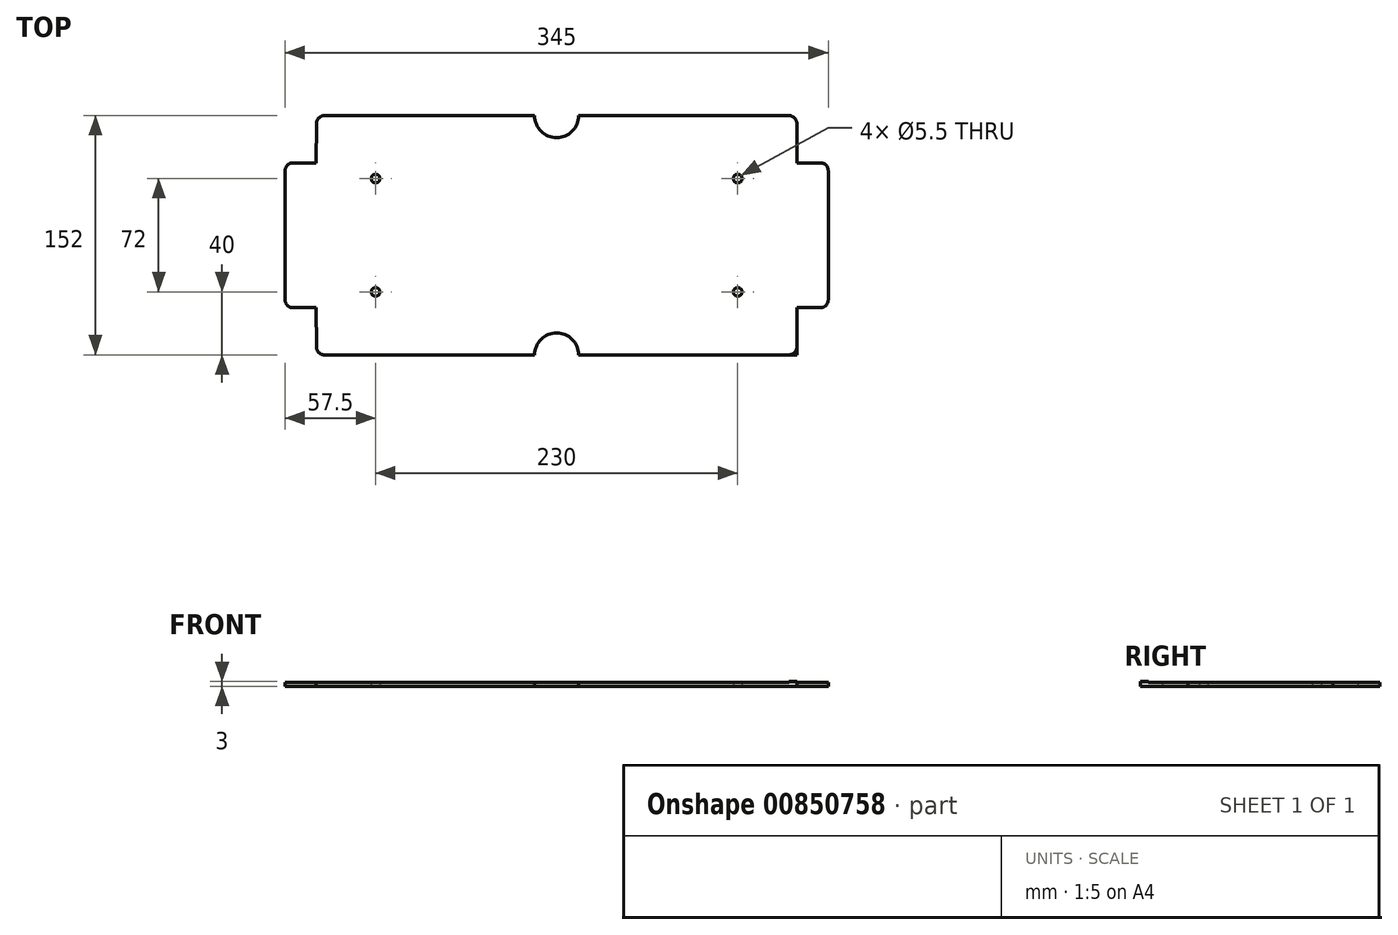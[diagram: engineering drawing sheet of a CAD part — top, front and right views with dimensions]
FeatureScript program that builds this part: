
annotation { "Feature Type Name" : "Feature", "Feature Type Description" : "" }
export const myFeature = defineFeature(function(context is Context, id is Id, definition is map)
    precondition{}
    {
        {
            var Q0;
            Q0=qCreatedBy(makeId("Top.planeOp"),FACE);
            var sketch = newSketch(context, id + "F0", { "sketchPlane" : qUnion([Q0])});
            skLineSegment(sketch, "E0.top", {"start": v(-147.54, -76) * mm, "end": v(152.5, -76) * mm});
            skLineSegment(sketch, "E0.right", {"start": v(172.5, 46) * mm, "end": v(172.5, -46) * mm});
            skPoint(sketch, "E0.middle", {"position": v(0, 0) * mm});
            skLineSegment(sketch, "E1", {"start": v(-152.5, 76) * mm, "end": v(152.5, 76) * mm});
            skLineSegment(sketch, "E2", {"start": v(-172.5, 41) * mm, "end": v(-172.5, -41) * mm});
            skLineSegment(sketch, "E3", {"start": v(-167.5, 46) * mm, "end": v(-152.75, 46) * mm});
            skLineSegment(sketch, "E4", {"start": v(-152.75, 46) * mm, "end": v(-152.5, 76) * mm});
            skLineSegment(sketch, "E5.MirrorCS", {"start": v(172.5, 46) * mm, "end": v(152.75, 46) * mm});
            skLineSegment(sketch, "E6.MirrorCS", {"start": v(152.75, 46) * mm, "end": v(152.5, 76) * mm});
            skLineSegment(sketch, "E7.MirrorCS", {"start": v(152.5, 76) * mm, "end": v(-152.5, 76) * mm});
            skPoint(sketch, "E8.orphan", {"position": v(-172.5, 76) * mm});
            skPoint(sketch, "E9.orphan", {"position": v(172.5, 76) * mm});
            skLineSegment(sketch, "E10.MirrorCS", {"start": v(-167.5, -46) * mm, "end": v(-152.75, -46) * mm});
            skLineSegment(sketch, "E11.MirrorCS", {"start": v(-152.75, -46) * mm, "end": v(-152.54, -71.04) * mm});
            skLineSegment(sketch, "E12.MirrorCS", {"start": v(152.75, -46) * mm, "end": v(152.5, -76) * mm});
            skLineSegment(sketch, "E13.MirrorCS", {"start": v(172.5, -46) * mm, "end": v(152.75, -46) * mm});
            skPoint(sketch, "E14.orphan", {"position": v(-172.5, -76) * mm});
            skPoint(sketch, "E15.orphan", {"position": v(172.5, -76) * mm});
            skPoint(sketch, "E16.visualSharp", {"position": v(-172.5, 46) * mm});
            skArc(sketch, "E16.filletArc", {"start": v(-167.5, 46) * mm, "mid": v(-171.04, 44.54) * mm, "end": v(-172.5, 41) * mm});
            skPoint(sketch, "E17.visualSharp", {"position": v(-172.5, -46) * mm});
            skArc(sketch, "E17.filletArc", {"start": v(-172.5, -41) * mm, "mid": v(-171.04, -44.54) * mm, "end": v(-167.5, -46) * mm});
            skPoint(sketch, "E18.visualSharp", {"position": v(-152.5, -76) * mm});
            skArc(sketch, "E18.filletArc", {"start": v(-152.54, -71.04) * mm, "mid": v(-151.06, -74.55) * mm, "end": v(-147.54, -76) * mm});
            skLineSegment(sketch, "E19.MirrorCS", {"start": v(172.5, 41) * mm, "end": v(172.5, -41) * mm});
            skLineSegment(sketch, "E20.MirrorCS", {"start": v(167.5, -46) * mm, "end": v(152.75, -46) * mm});
            skLineSegment(sketch, "E21.MirrorCS", {"start": v(152.75, -46) * mm, "end": v(152.54, -71.04) * mm});
            skArc(sketch, "E22.MirrorCS", {"start": v(172.5, -41) * mm, "mid": v(171.04, -44.54) * mm, "end": v(167.5, -46) * mm});
            skArc(sketch, "E23.MirrorCS", {"start": v(152.54, -71.04) * mm, "mid": v(151.06, -74.55) * mm, "end": v(147.54, -76) * mm});
            skArc(sketch, "E24.MirrorCS", {"start": v(167.5, 46) * mm, "mid": v(171.04, 44.54) * mm, "end": v(172.5, 41) * mm});
            skArc(sketch, "E25.MirrorCS", {"start": v(152.54, 71.04) * mm, "mid": v(151.06, 74.55) * mm, "end": v(147.54, 76) * mm});
            skArc(sketch, "E26.MirrorCS", {"start": v(-152.54, 71.04) * mm, "mid": v(-151.06, 74.55) * mm, "end": v(-147.54, 76) * mm});
            skPoint(sketch, "E27", {"position": v(0, 76) * mm});
            skPoint(sketch, "E28", {"position": v(0, -76) * mm});
            skPoint(sketch, "E29", {"position": v(-115, -36) * mm});
            skPoint(sketch, "E30.MirrorP", {"position": v(115, -36) * mm});
            skPoint(sketch, "E31.MirrorP", {"position": v(-115, 36) * mm});
            skPoint(sketch, "E32.MirrorP", {"position": v(115, 36) * mm});
            skSolve(sketch);
        }
        {
            var Q0;
            Q0=makeQuery(id+"F0.imprint","IMPRINT",FACE,{"disambiguationData":[TD([[makeQuery(id+"F0.imprint","IMPRINT",EDGE,{"derivedFrom":sQuery(id+"F0.wireOp",EDGE,"E0.top")}),1.0]])]});
            extrude(context, id + "F1", {"entities" : qUnion([Q0]), "depth" : 3 * mm, "offsetDistance" : 25 * mm});
        }
        {
            var Q0;
            Q0=makeQuery(id+"F0.imprint","IMPRINT",FACE,{"disambiguationData":[TD([[makeQuery(id+"F0.imprint","IMPRINT",EDGE,{"derivedFrom":sQuery(id+"F0.wireOp",EDGE,"E2")}),1.0]])]});
            extrude(context, id + "F2", {"entities" : qUnion([Q0]), "operationType" : NewBodyOperationType.ADD, "depth" : 2.5 * mm, "offsetDistance" : 25 * mm});
        }
        {
            var Q0;
            Q0=sQuery(id+"F0.wireOp",VERTEX,"E27");
            var Q1;
            Q1=makeQuery(id+"F1.opExtrude","SWEPT_BODY",BODY,{"disambiguationData":[OSD([sQuery(id+"F0.wireOp",EDGE,"E0.top"),sQuery(id+"F0.wireOp",EDGE,"E12.MirrorCS"),sQuery(id+"F0.wireOp",EDGE,"E23.MirrorCS")])]});
            hole(context, id + "F3", {"style" : HoleStyle.SIMPLE, "endStyle" : HoleEndStyle.BLIND, "oppositeDirection" : true, "holeDiameter" : 28 * mm, "majorDiameter" : 5 * mm, "holeDepth" : 50.5 * mm, "isTappedThrough" : true, "tappedDepth" : 20 * mm, "tapClearance" : 3, "locations" : qUnion([Q0]), "scope" : qUnion([Q1])});
        }
        {
            var Q0;
            Q0=sQuery(id+"F0.wireOp",VERTEX,"E28");
            var Q1;
            Q1=makeQuery(id+"F1.opExtrude","SWEPT_BODY",BODY,{"disambiguationData":[OSD([sQuery(id+"F0.wireOp",EDGE,"E0.top"),sQuery(id+"F0.wireOp",EDGE,"E12.MirrorCS"),sQuery(id+"F0.wireOp",EDGE,"E23.MirrorCS")])]});
            hole(context, id + "F4", {"style" : HoleStyle.SIMPLE, "endStyle" : HoleEndStyle.BLIND, "oppositeDirection" : true, "holeDiameter" : 28 * mm, "majorDiameter" : 5 * mm, "holeDepth" : 50.5 * mm, "isTappedThrough" : true, "tappedDepth" : 20 * mm, "tapClearance" : 3, "locations" : qUnion([Q0]), "scope" : qUnion([Q1])});
        }
        {
            var Q0;
            Q0=sQuery(id+"F0.wireOp",VERTEX,"E29");
            var Q1;
            Q1=sQuery(id+"F0.wireOp",VERTEX,"E31.MirrorP");
            var Q2;
            Q2=sQuery(id+"F0.wireOp",VERTEX,"E32.MirrorP");
            var Q3;
            Q3=sQuery(id+"F0.wireOp",VERTEX,"E30.MirrorP");
            var Q4;
            Q4=makeQuery(id+"F1.opExtrude","SWEPT_BODY",BODY,{"disambiguationData":[OSD([sQuery(id+"F0.wireOp",EDGE,"E0.top"),sQuery(id+"F0.wireOp",EDGE,"E12.MirrorCS"),sQuery(id+"F0.wireOp",EDGE,"E23.MirrorCS")])]});
            hole(context, id + "F5", {"style" : HoleStyle.SIMPLE, "endStyle" : HoleEndStyle.BLIND, "oppositeDirection" : true, "standardTappedOrClearance" : lookupTablePath({ "fit" : "Normal", "standard" : "ISO", "size" : "M5", "type" : "Clearance" }), "standardBlindInLast" : lookupTablePath({ "fit" : "Normal", "standard" : "ISO", "size" : "M5", "type" : "Clearance" }), "holeDiameter" : 5.5 * mm, "majorDiameter" : 5 * mm, "holeDepth" : 14.4 * mm, "isTappedThrough" : true, "tappedDepth" : 12 * mm, "tapClearance" : 3, "locations" : qUnion([Q0, Q1, Q2, Q3]), "scope" : qUnion([Q4])});
        }
    });
